# Revit family: Haworth_Lyda_Bench_Hexagon
name_source: partatom
category: Furniture
revit_build: Autodesk Revit 2018 (Build: 20170223_1515(x64)
units: mm (PartAtom-declared; Revit-internal decimal feet)

## family parameters
Always vertical = Yes
Cut with Voids When Loaded = No
OmniClass Number = 23.40.70.14.64.21
OmniClass Title = Systems Furniture
Room Calculation Point = No
Shared = No
Work Plane-Based = No

## types (1)
- Hexagon Bench
    Actual Depth = 41"
    Actual Height = 17"
    Actual Width = 50 1/2"
    Assembly Code = E2020200
    Description = Haworth - Lyda - Bench - Hexagon
    Leg Finish = Haworth _ Paint _ Black
    Manufacturer = Haworth
    Model = HCCL-LYBH-L11X
    Revision Number = 1
    Size = Verify Final Dim. w/ Haworth
    Standard Depth = 41 in
    Standard Width = 50.5 in
    Sustainability Info = https://www.haworth.com
    URL = www.haworth.com
    URL - Product = https://www.haworth.com
    Warranty = http://www.haworth.com

## geometry (parser evidence)
native form markers: Sweep x9
no freeform markers — native parametric forms only
